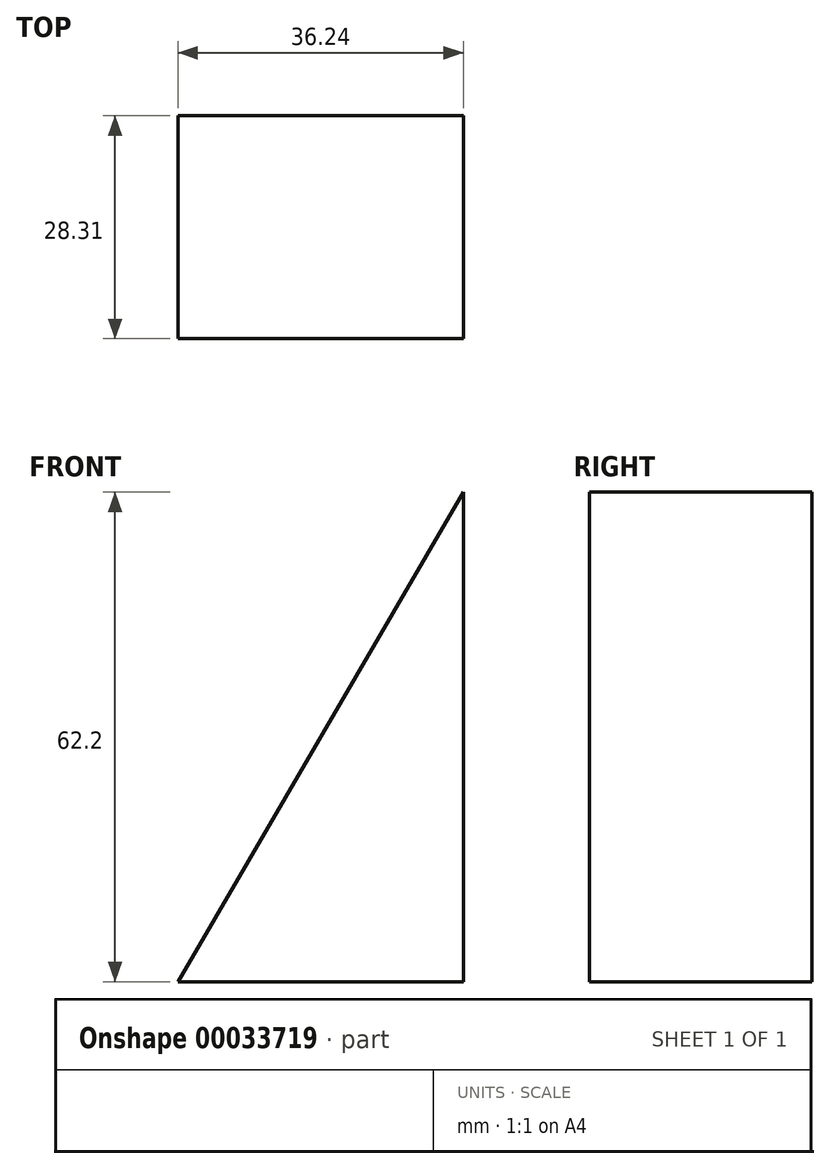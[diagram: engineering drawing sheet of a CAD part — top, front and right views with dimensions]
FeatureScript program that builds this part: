
annotation { "Feature Type Name" : "Feature", "Feature Type Description" : "" }
export const myFeature = defineFeature(function(context is Context, id is Id, definition is map)
    precondition{}
    {
        {
            var Q0;
            Q0=qCreatedBy(makeId("Front.planeOp"),FACE);
            var sketch = newSketch(context, id + "F2", { "sketchPlane" : qUnion([Q0])});
            skLineSegment(sketch, "E0", {"start": v(-36.24, 0) * mm, "end": v(-36.24, 0) * mm});
            skLineSegment(sketch, "E1", {"start": v(-36.24, 0) * mm, "end": v(0, 0) * mm});
            skLineSegment(sketch, "E2", {"start": v(0, 0) * mm, "end": v(0, 62.2) * mm});
            skLineSegment(sketch, "E3", {"start": v(0, 62.2) * mm, "end": v(-36.24, 0) * mm});
            skSolve(sketch);
        }
        {
            var Q0;
            Q0 = qSketchRegion(id + "F2", true);
            var Q1;
            Q1=makeQuery(id+"F2.imprint","IMPRINT",FACE,{"disambiguationData":[TD([[makeQuery(id+"F2.imprint","IMPRINT",EDGE,{"derivedFrom":sQuery(id+"F2.wireOp",EDGE,"E1")}),1.0]])]});
            extrude(context, id + "F0", {"entities" : qUnion([Q0, Q1]), "depth" : 28.3 * mm});
        }
    });
